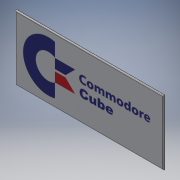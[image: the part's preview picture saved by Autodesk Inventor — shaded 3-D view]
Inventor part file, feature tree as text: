
AUTODESK INVENTOR PART (.ipt)
format: ipt  version: 2018 (Build 220112000, 112)  size: 131,072 bytes
history: native  units: in
note: dims shown in document units (in); Inventor stores cm internally (conversion verified against a paired STEP export)
features: other x5, sketch x3, extrude x2, fillet x1, reference x1, projected_geometry x1
ambient origin geometry x8: Origin, YZ Plane, XZ Plane, XY Plane, X Axis, Y Axis, Z Axis, Center Point
bodies: Solid1 (feature_tree)
feature tree (13):
  extrude  "Extrusion1"  Depth=0.005in TaperAngle=0.0deg
  extrude  "Extrusion2"  [1 undecoded]
  fillet  "Fillet1"  [1 undecoded]
  other  "Decal1"
  sketch  "Sketch1"  dims[d0=0.001in d1=0.0in d2=0.005in d3=0.0in]
  reference  "Reference1"
  sketch  "Sketch2"  dims[d4=0.005in]
  projected_geometry  "Projected Loop1"
  sketch  "Sketch3"
  other  "Image1"
  other  "<userpath>\Documents\Commodore Cube Project\Case\Assembly.iam"
  other  "Assembly.iam"
  other  "Dome:1"
note: 2 required parameter values undecoded (feature->parameter linkage not recoverable at this tier; creation-order binding heuristic only, values carry confidence <= 0.55)
